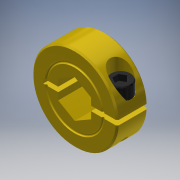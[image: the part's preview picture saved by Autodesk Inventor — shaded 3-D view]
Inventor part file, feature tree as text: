
AUTODESK INVENTOR PART (.ipt)
format: ipt  version: 2017.1 (Build 211199000, 199)  size: 304,128 bytes
history: native  units: in
note: dims shown in document units (in); Inventor stores cm internally (conversion verified against a paired STEP export)
features: extrude x2, sketch x2, other x1, imported_body x1
ambient origin geometry x8: Origin, YZ Plane, XZ Plane, XY Plane, X Axis, Y Axis, Z Axis, Center Point
bodies: Solid1 (feature_tree)
feature tree (6):
  other  "CL-8-A1"
  extrude  "Extrusion1"  Depth=0.4375in TaperAngle=0.0deg
  extrude  "Extrusion2"  [1 undecoded]
  imported_body  "Base1"
  sketch  "Sketch2"  dims[d0=0.5in d1=0.4375in d2=0.0in]
  sketch  "Sketch3"  dims[d3=1.0in d4=0.0in]
note: 1 required parameter value undecoded (feature->parameter linkage not recoverable at this tier; creation-order binding heuristic only, values carry confidence <= 0.55)
